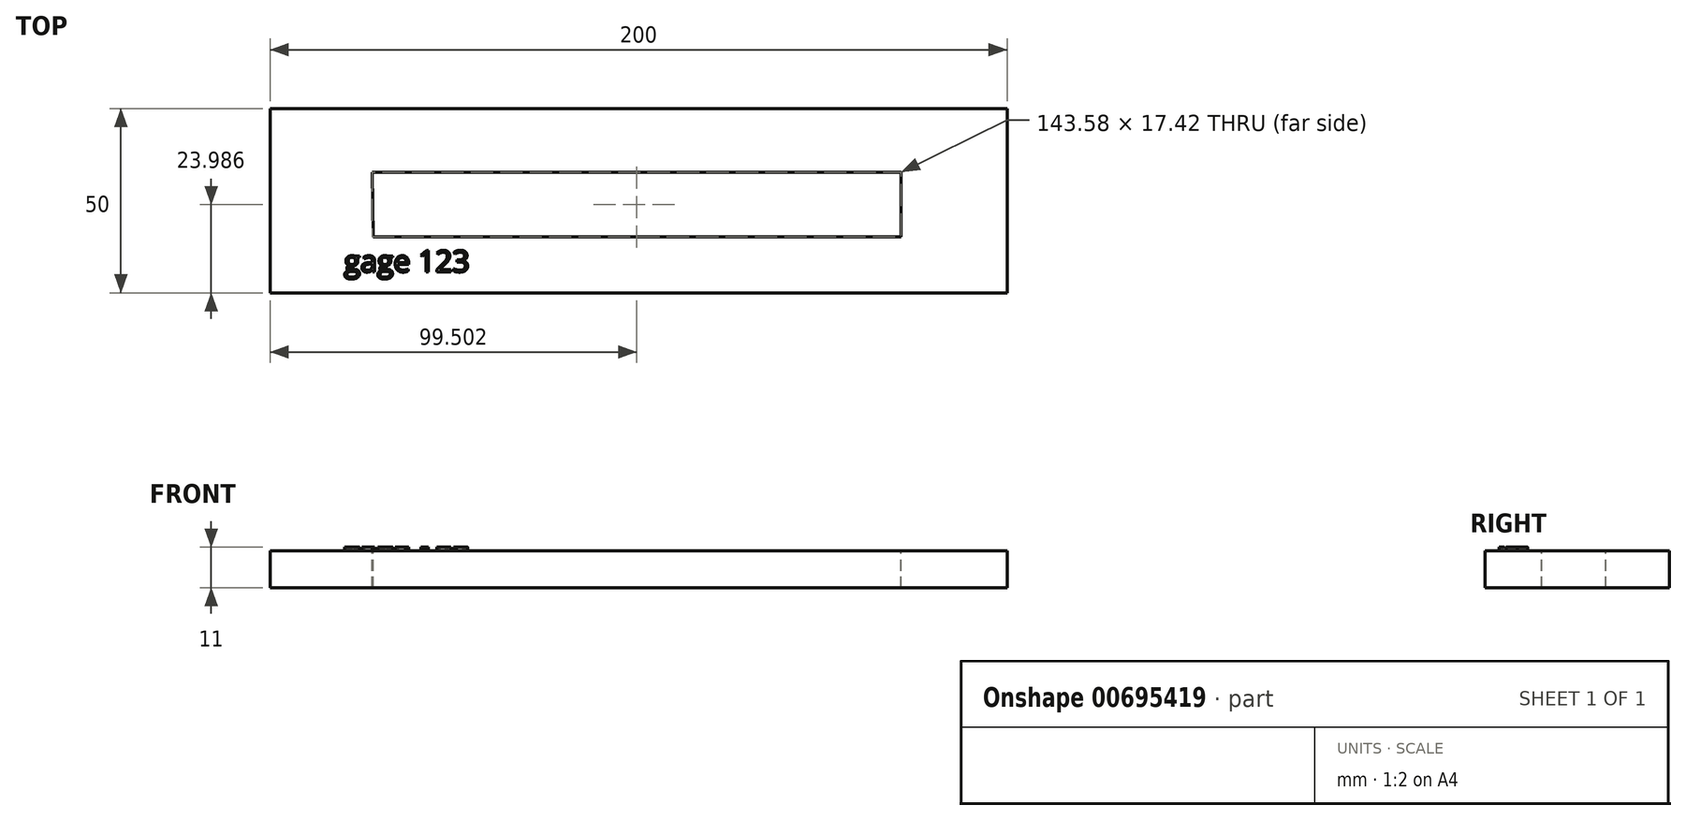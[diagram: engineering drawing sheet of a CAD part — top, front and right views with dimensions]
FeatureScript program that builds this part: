
annotation { "Feature Type Name" : "Feature", "Feature Type Description" : "" }
export const myFeature = defineFeature(function(context is Context, id is Id, definition is map)
    precondition{}
    {
        {
            var Q0;
            Q0=qCreatedBy(makeId("Top.planeOp"),FACE);
            var sketch = newSketch(context, id + "F0", { "sketchPlane" : qUnion([Q0])});
            skLineSegment(sketch, "E0.bottom", {"start": v(-95.74, 6.85) * mm, "end": v(104.26, 6.85) * mm});
            skLineSegment(sketch, "E0.top", {"start": v(-95.74, -43.15) * mm, "end": v(104.26, -43.15) * mm});
            skLineSegment(sketch, "E0.left", {"start": v(-95.74, 6.85) * mm, "end": v(-95.74, -43.15) * mm});
            skLineSegment(sketch, "E0.right", {"start": v(104.26, 6.85) * mm, "end": v(104.26, -43.15) * mm});
            skSolve(sketch);
        }
        {
            var Q0;
            Q0 = qSketchRegion(id + "F0", true);
            extrude(context, id + "F1", {"entities" : qUnion([Q0]), "depth" : 10 * mm, "offsetDistance" : 25 * mm});
        }
        {
            var Q0;
            Q0=makeQuery(id+"F1.opExtrude","CAP_FACE",FACE,{"disambiguationData":[OSD([sQuery(id+"F0.wireOp",EDGE,"E0.bottom"),sQuery(id+"F0.wireOp",EDGE,"E0.top"),sQuery(id+"F0.wireOp",EDGE,"E0.left"),sQuery(id+"F0.wireOp",EDGE,"E0.right")])],"isStart":false});
            var sketch = newSketch(context, id + "F2", { "sketchPlane" : qUnion([Q0])});
            skLineSegment(sketch, "E1", {"start": v(-67.72, -27.88) * mm, "end": v(75.55, -27.88) * mm});
            skLineSegment(sketch, "E2", {"start": v(75.55, -27.88) * mm, "end": v(75.55, -10.45) * mm});
            skLineSegment(sketch, "E3", {"start": v(75.55, -10.45) * mm, "end": v(-68.03, -10.45) * mm});
            skLineSegment(sketch, "E4", {"start": v(-68.03, -10.45) * mm, "end": v(-67.72, -27.88) * mm});
            skSolve(sketch);
        }
        {
            var Q0;
            Q0=makeQuery(id+"F2.imprint","IMPRINT",FACE,{"disambiguationData":[TD([[makeQuery(id+"F2.imprint","IMPRINT",EDGE,{"derivedFrom":sQuery(id+"F2.wireOp",EDGE,"E1")}),1.0]])]});
            extrude(context, id + "F3", {"entities" : qUnion([Q0]), "operationType" : NewBodyOperationType.REMOVE, "oppositeDirection" : true, "depth" : 25 * mm, "offsetDistance" : 25 * mm});
        }
        {
            var Q0;
            Q0=makeQuery(id+"F1.opExtrude","CAP_FACE",FACE,{"disambiguationData":[OSD([sQuery(id+"F0.wireOp",EDGE,"E0.bottom"),sQuery(id+"F0.wireOp",EDGE,"E0.top"),sQuery(id+"F0.wireOp",EDGE,"E0.left"),sQuery(id+"F0.wireOp",EDGE,"E0.right")])],"isStart":false});
            var sketch = newSketch(context, id + "F4", { "sketchPlane" : qUnion([Q0])});
            skText(sketch, "E5", { "text": "gage 123", "fontName": "OpenSans-Regular.ttf"});
            const initialGuessF4  = {"E5": [-0.07566, -0.03745, 1, 0, 0.00585]};
            skSetInitialGuess(sketch, initialGuessF4);
            skSolve(sketch);
        }
        {
            var Q0;
            Q0 = qSketchRegion(id + "F4", true);
            extrude(context, id + "F5", {"entities" : qUnion([Q0]), "operationType" : NewBodyOperationType.ADD, "depth" : 1 * mm, "offsetDistance" : 25 * mm});
        }
    });
